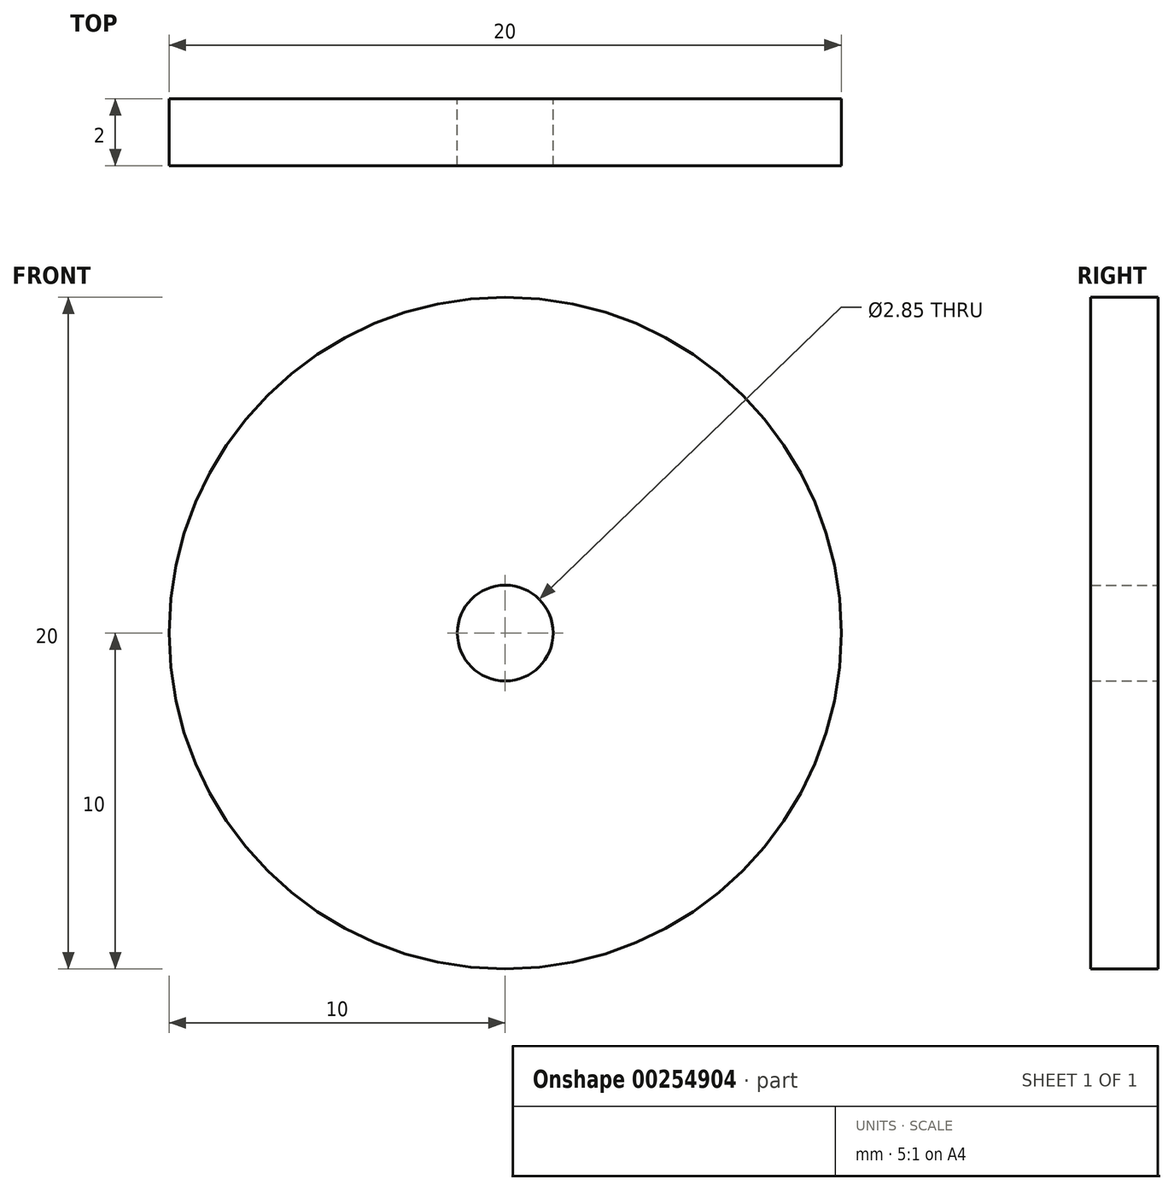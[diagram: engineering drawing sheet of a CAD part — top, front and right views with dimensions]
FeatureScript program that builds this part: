
annotation { "Feature Type Name" : "Feature", "Feature Type Description" : "" }
export const myFeature = defineFeature(function(context is Context, id is Id, definition is map)
    precondition{}
    {
        {
            var Q0;
            Q0=qCreatedBy(makeId("Front.planeOp"),FACE);
            var sketch = newSketch(context, id + "F0", { "sketchPlane" : qUnion([Q0])});
            skCircle(sketch, "E0", {"center": v(0, 0) * mm, "radius": 10 * mm});
            skCircle(sketch, "E1", {"center": v(0, 0) * mm, "radius": 1.43 * mm});
            skSolve(sketch);
        }
        {
            var Q0;
            Q0=makeQuery(id+"F0.imprint","IMPRINT",FACE,{"disambiguationData":[TD([[makeQuery(id+"F0.imprint","IMPRINT",EDGE,{"derivedFrom":sQuery(id+"F0.wireOp",EDGE,"E0")}),1.0]])]});
            extrude(context, id + "F1", {"entities" : qUnion([Q0]), "depth" : 2 * mm});
        }
    });
